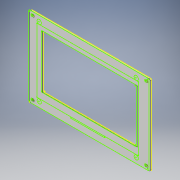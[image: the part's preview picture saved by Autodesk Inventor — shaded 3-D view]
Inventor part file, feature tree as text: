
AUTODESK INVENTOR PART (.ipt)
format: ipt  version: 2019 (Build 230136000, 136)  size: 192,512 bytes
history: native  units: in
note: dims shown in document units (in); Inventor stores cm internally (conversion verified against a paired STEP export)
features: sketch x2, projected_geometry x2, imported_body x1
ambient origin geometry x8: Origin, YZ Plane, XZ Plane, XY Plane, X Axis, Y Axis, Z Axis, Center Point
bodies: Solid1 (feature_tree)
feature tree (5):
  imported_body  "Base1"
  sketch  "Sketch2"
  sketch  "Sketch3"
  projected_geometry  "Projected Loop1"
  projected_geometry  "Projected Loop2"
